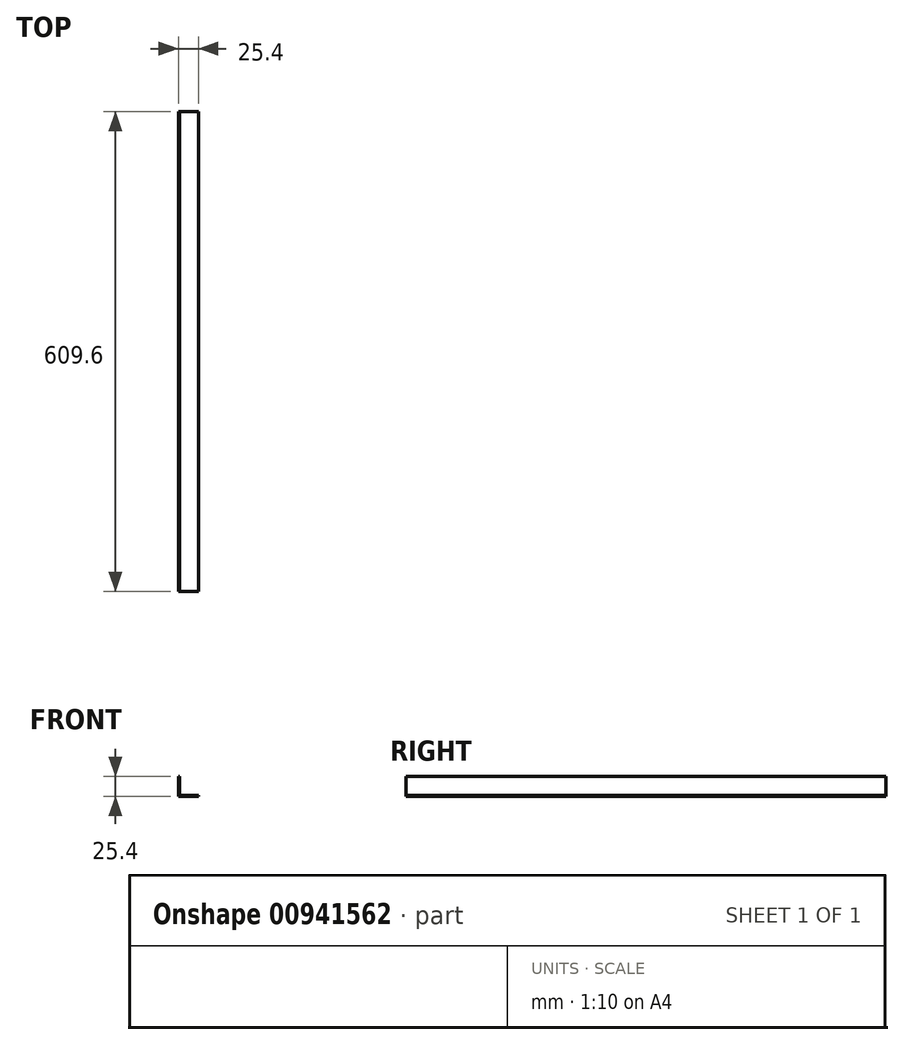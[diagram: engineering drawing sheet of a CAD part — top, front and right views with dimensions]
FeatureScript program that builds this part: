
annotation { "Feature Type Name" : "Feature", "Feature Type Description" : "" }
export const myFeature = defineFeature(function(context is Context, id is Id, definition is map)
    precondition{}
    {
        {
            var Q0;
            Q0=qCreatedBy(makeId("Front.planeOp"),FACE);
            var sketch = newSketch(context, id + "F0", { "sketchPlane" : qUnion([Q0])});
            skLineSegment(sketch, "E0", {"start": v(0, 0) * mm, "end": v(0, 25.4) * mm});
            skLineSegment(sketch, "E1", {"start": v(0, 0) * mm, "end": v(25.4, 0) * mm});
            skLineSegment(sketch, "E2.0", {"start": v(1.59, 1.59) * mm, "end": v(1.59, 25.4) * mm});
            skLineSegment(sketch, "E3.0", {"start": v(1.59, 1.59) * mm, "end": v(25.4, 1.59) * mm});
            skLineSegment(sketch, "E4", {"start": v(0, 25.4) * mm, "end": v(1.59, 25.4) * mm});
            skLineSegment(sketch, "E5", {"start": v(25.4, 1.59) * mm, "end": v(25.4, 0) * mm});
            skSolve(sketch);
        }
        {
            var Q0;
            Q0 = qSketchRegion(id + "F0", true);
            extrude(context, id + "F1", {"entities" : qUnion([Q0]), "depth" : 609.6 * mm, "offsetDistance" : 25.4 * mm});
        }
    });
